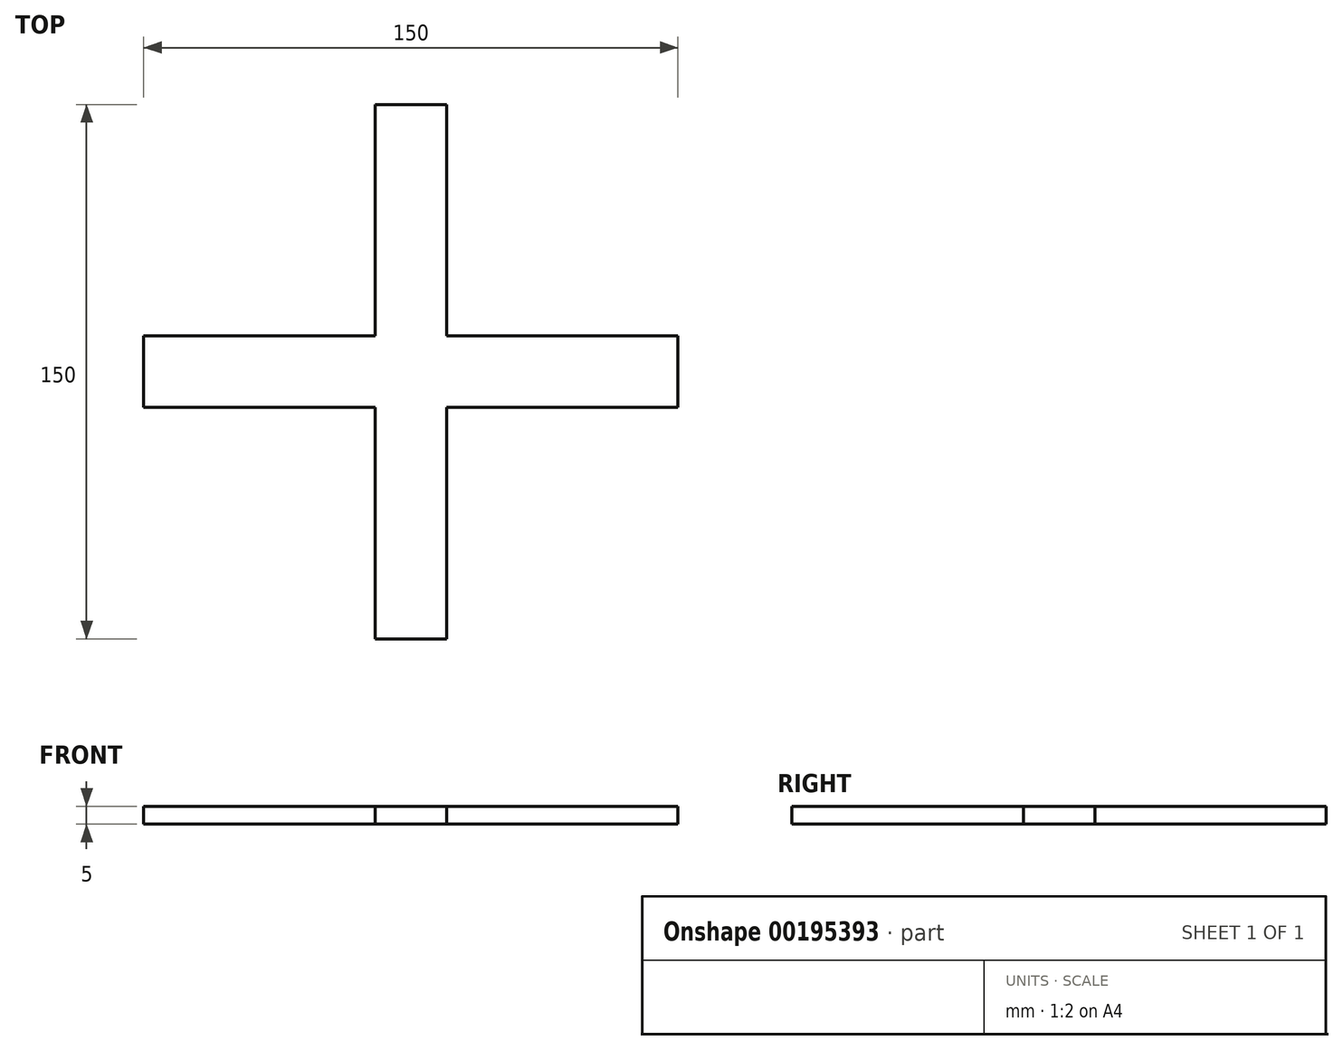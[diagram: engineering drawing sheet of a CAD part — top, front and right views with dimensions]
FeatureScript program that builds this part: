
annotation { "Feature Type Name" : "Feature", "Feature Type Description" : "" }
export const myFeature = defineFeature(function(context is Context, id is Id, definition is map)
    precondition{}
    {
        {
            var Q0;
            Q0=qCreatedBy(makeId("Top.planeOp"),FACE);
            var sketch = newSketch(context, id + "F0", { "sketchPlane" : qUnion([Q0])});
            skLineSegment(sketch, "E0.bottom", {"start": v(-10, 75) * mm, "end": v(10, 75) * mm});
            skLineSegment(sketch, "E0.top", {"start": v(-10, -75) * mm, "end": v(10, -75) * mm});
            skLineSegment(sketch, "E0.left", {"start": v(-10, 75) * mm, "end": v(-10, 10) * mm});
            skLineSegment(sketch, "E0.right", {"start": v(10, 75) * mm, "end": v(10, 10) * mm});
            skPoint(sketch, "E0.middle", {"position": v(0, 0) * mm});
            skLineSegment(sketch, "E1.bottom", {"start": v(-75, 10) * mm, "end": v(-10, 10) * mm});
            skLineSegment(sketch, "E1.top", {"start": v(-75, -10) * mm, "end": v(-10, -10) * mm});
            skLineSegment(sketch, "E1.left", {"start": v(-75, 10) * mm, "end": v(-75, -10) * mm});
            skLineSegment(sketch, "E1.right", {"start": v(75, 10) * mm, "end": v(75, -10) * mm});
            skLineSegment(sketch, "E2.trimOffspring", {"start": v(-10, -10) * mm, "end": v(-10, -75) * mm});
            skLineSegment(sketch, "E3.trimOffspring", {"start": v(10, 10) * mm, "end": v(75, 10) * mm});
            skLineSegment(sketch, "E4.trimOffspring", {"start": v(10, -10) * mm, "end": v(10, -75) * mm});
            skLineSegment(sketch, "E5.trimOffspring", {"start": v(10, -10) * mm, "end": v(75, -10) * mm});
            skSolve(sketch);
        }
        {
            var Q0;
            Q0 = qSketchRegion(id + "F0", true);
            extrude(context, id + "F1", {"entities" : qUnion([Q0]), "depth" : 5 * mm});
        }
    });
